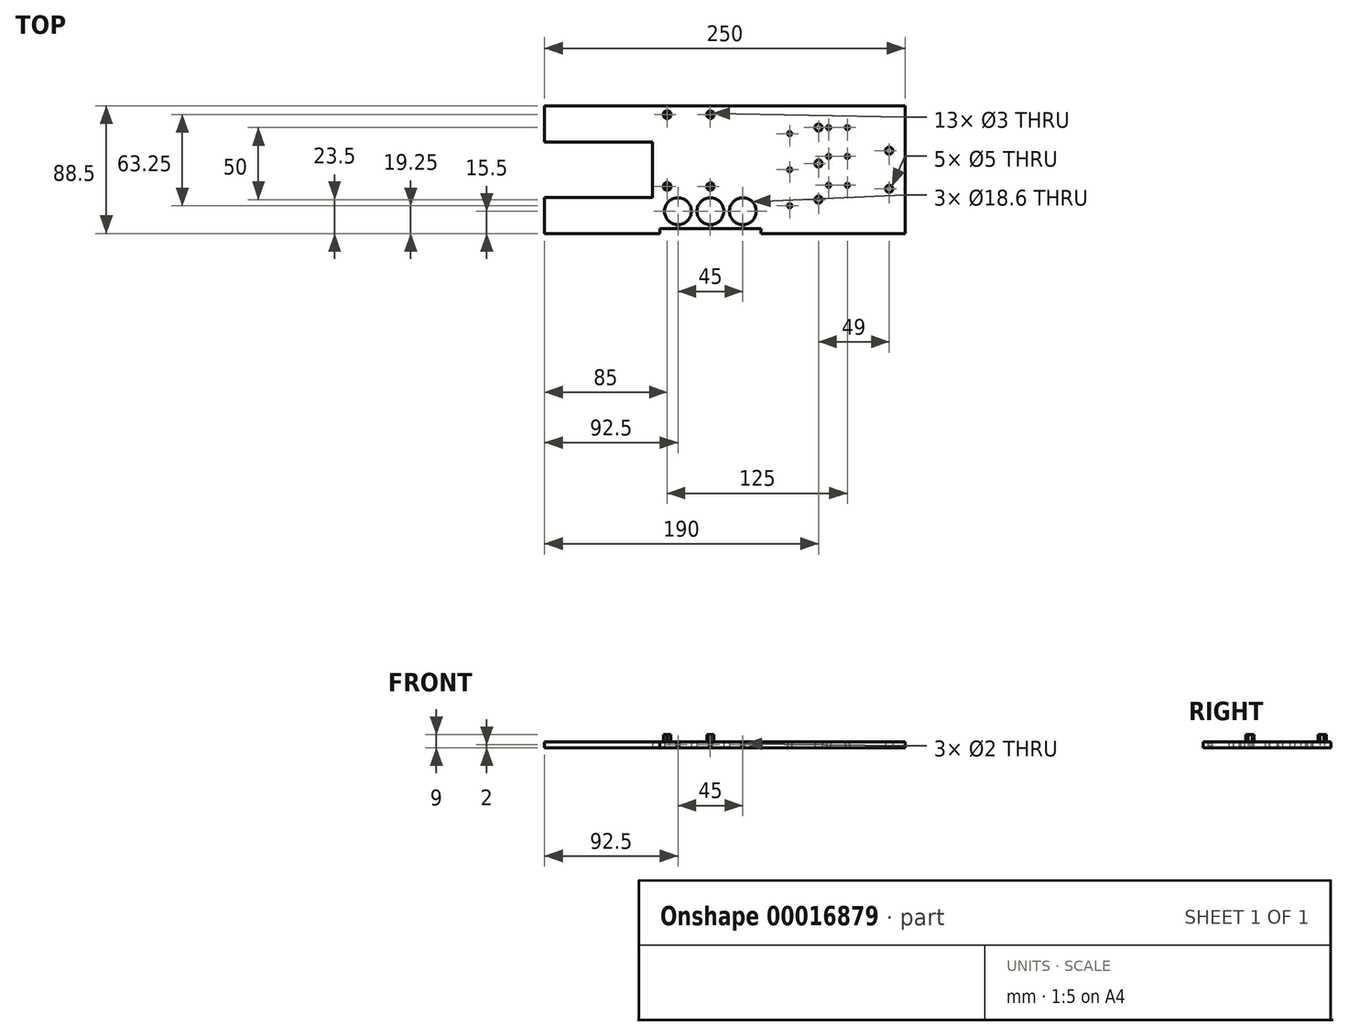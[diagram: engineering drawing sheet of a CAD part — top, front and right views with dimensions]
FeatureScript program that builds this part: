
annotation { "Feature Type Name" : "Feature", "Feature Type Description" : "" }
export const myFeature = defineFeature(function(context is Context, id is Id, definition is map)
    precondition{}
    {
        {
            var Q0;
            Q0=qCreatedBy(makeId("Top.planeOp"),FACE);
            var sketch = newSketch(context, id + "F0", { "sketchPlane" : qUnion([Q0])});
            skLineSegment(sketch, "E0", {"start": v(0, 0) * mm, "end": v(80, 0) * mm});
            skLineSegment(sketch, "E1", {"start": v(80, 0) * mm, "end": v(80, 3.5) * mm});
            skLineSegment(sketch, "E2", {"start": v(80, 3.5) * mm, "end": v(150, 3.5) * mm});
            skLineSegment(sketch, "E3", {"start": v(150, 3.5) * mm, "end": v(150, 0) * mm});
            skLineSegment(sketch, "E4", {"start": v(150, 0) * mm, "end": v(250, 0) * mm});
            skLineSegment(sketch, "E5", {"start": v(250, 0) * mm, "end": v(250, 88.5) * mm});
            skLineSegment(sketch, "E6", {"start": v(250, 88.5) * mm, "end": v(0, 88.5) * mm});
            skLineSegment(sketch, "E7", {"start": v(0, 88.5) * mm, "end": v(0, 63.5) * mm});
            skLineSegment(sketch, "E8", {"start": v(0, 63.5) * mm, "end": v(75, 63.5) * mm});
            skLineSegment(sketch, "E9", {"start": v(75, 63.5) * mm, "end": v(75, 25) * mm});
            skLineSegment(sketch, "E10", {"start": v(75, 25) * mm, "end": v(0, 25) * mm});
            skLineSegment(sketch, "E11", {"start": v(0, 25) * mm, "end": v(0, 0) * mm});
            skCircle(sketch, "E12", {"center": v(92.5, 15.5) * mm, "radius": 9.3 * mm});
            skCircle(sketch, "E13", {"center": v(115, 15.5) * mm, "radius": 9.3 * mm});
            skCircle(sketch, "E14", {"center": v(137.5, 15.5) * mm, "radius": 9.3 * mm});
            skCircle(sketch, "E15", {"center": v(239, 57.5) * mm, "radius": 2.5 * mm});
            skCircle(sketch, "E16", {"center": v(239, 31) * mm, "radius": 2.5 * mm});
            skCircle(sketch, "E17", {"center": v(197, 73.5) * mm, "radius": 1.5 * mm});
            skCircle(sketch, "E18", {"center": v(210, 73.5) * mm, "radius": 1.5 * mm});
            skLineSegment(sketch, "E19", {"start": v(250, 44.25) * mm, "end": v(-80.74, 44.25) * mm, "construction": true});
            skCircle(sketch, "E20.MirrorC", {"center": v(197, 33.5) * mm, "radius": 1.5 * mm});
            skCircle(sketch, "E21.MirrorC", {"center": v(210, 33.5) * mm, "radius": 1.5 * mm});
            skCircle(sketch, "E22", {"center": v(197, 53.5) * mm, "radius": 1.5 * mm});
            skCircle(sketch, "E23", {"center": v(210, 53.5) * mm, "radius": 1.5 * mm});
            skCircle(sketch, "E24", {"center": v(190, 73.5) * mm, "radius": 2.5 * mm});
            skCircle(sketch, "E25", {"center": v(190, 48.5) * mm, "radius": 2.5 * mm});
            skCircle(sketch, "E26", {"center": v(190, 23.5) * mm, "radius": 2.5 * mm});
            skCircle(sketch, "E27", {"center": v(170, 19.25) * mm, "radius": 1.5 * mm});
            skCircle(sketch, "E28", {"center": v(170, 44.25) * mm, "radius": 1.5 * mm});
            skCircle(sketch, "E29", {"center": v(170, 69.25) * mm, "radius": 1.5 * mm});
            skSolve(sketch);
        }
        {
            var Q0;
            Q0 = qSketchRegion(id + "F0", true);
            extrude(context, id + "F1", {"entities" : qUnion([Q0]), "depth" : 4 * mm});
        }
        {
            var Q0;
            Q0=makeQuery(id+"F1.opExtrude","SWEPT_FACE",FACE,{"disambiguationData":[OSD([sQuery(id+"F0.wireOp",EDGE,"E2")])]});
            var sketch = newSketch(context, id + "F2", { "sketchPlane" : qUnion([Q0])});
            skPoint(sketch, "E30.0", {"position": v(92.5, 0) * mm});
            skPoint(sketch, "E30.1", {"position": v(115, 0) * mm});
            skPoint(sketch, "E30.2", {"position": v(137.5, 0) * mm});
            skCircle(sketch, "E31", {"center": v(92.5, 2) * mm, "radius": 1 * mm});
            skCircle(sketch, "E32", {"center": v(115, 2) * mm, "radius": 1 * mm});
            skCircle(sketch, "E33", {"center": v(137.5, 2) * mm, "radius": 1 * mm});
            skSolve(sketch);
        }
        {
            var Q0;
            Q0 = qSketchRegion(id + "F2", true);
            extrude(context, id + "F3", {"entities" : qUnion([Q0]), "operationType" : NewBodyOperationType.REMOVE, "endBound" : BoundingType.UP_TO_NEXT, "oppositeDirection" : true, "depth" : 25 * mm});
        }
        {
            var Q0;
            Q0=makeQuery(id+"F1.opExtrude","CAP_FACE",FACE,{"disambiguationData":[OSD([sQuery(id+"F0.wireOp",EDGE,"E0"),sQuery(id+"F0.wireOp",EDGE,"E1"),sQuery(id+"F0.wireOp",EDGE,"E2"),sQuery(id+"F0.wireOp",EDGE,"E3"),sQuery(id+"F0.wireOp",EDGE,"E4"),sQuery(id+"F0.wireOp",EDGE,"E5"),sQuery(id+"F0.wireOp",EDGE,"E6"),sQuery(id+"F0.wireOp",EDGE,"E7"),sQuery(id+"F0.wireOp",EDGE,"E8"),sQuery(id+"F0.wireOp",EDGE,"E9"),sQuery(id+"F0.wireOp",EDGE,"E10"),sQuery(id+"F0.wireOp",EDGE,"E11"),sQuery(id+"F0.wireOp",EDGE,"E12"),sQuery(id+"F0.wireOp",EDGE,"E13"),sQuery(id+"F0.wireOp",EDGE,"E14"),sQuery(id+"F0.wireOp",EDGE,"E15"),sQuery(id+"F0.wireOp",EDGE,"E16"),sQuery(id+"F0.wireOp",EDGE,"4a421984-388c-4778-8cfd-64b2ba2534b6"),sQuery(id+"F0.wireOp",EDGE,"E17"),sQuery(id+"F0.wireOp",EDGE,"402fa86f-9143-4b8b-a13e-71166aee82f4"),sQuery(id+"F0.wireOp",EDGE,"E18"),sQuery(id+"F0.wireOp",EDGE,"9f3e0d40-b936-4480-b454-21914f751cbb"),sQuery(id+"F0.wireOp",EDGE,"ea4070be-86ac-4e07-94dc-6d67086c7fd0"),sQuery(id+"F0.wireOp",EDGE,"431228db-7fc8-4f03-8ea2-0f4400f562ce0.MirrorC"),sQuery(id+"F0.wireOp",EDGE,"53232193-0ba7-4fe3-a71a-7f03452151850.MirrorC"),sQuery(id+"F0.wireOp",EDGE,"E20.MirrorC"),sQuery(id+"F0.wireOp",EDGE,"E21.MirrorC"),sQuery(id+"F0.wireOp",EDGE,"28b9a74f-4e13-4495-a41d-af9b40233b3c0.MirrorC"),sQuery(id+"F0.wireOp",EDGE,"95b830d9-cd3e-44bb-837a-3bef2442fca50.MirrorC"),sQuery(id+"F0.wireOp",EDGE,"101621b3-3997-46f1-9346-ad9f52fe62e3"),sQuery(id+"F0.wireOp",EDGE,"5d99ffdf-71ce-4d62-a65a-32a693a247e0"),sQuery(id+"F0.wireOp",EDGE,"72875ce8-6458-4410-bd34-e62cef469ffd"),sQuery(id+"F0.wireOp",EDGE,"1edcefaf-f632-4f50-8d4d-05e26532ecec"),sQuery(id+"F0.wireOp",EDGE,"0031e8d8-416b-4e22-89b7-db54a3127eba0.MirrorC"),sQuery(id+"F0.wireOp",EDGE,"c55a97cf-9bee-4432-8ab8-8a13ee360a9b0.MirrorC")])],"isStart":false});
            var sketch = newSketch(context, id + "F4", { "sketchPlane" : qUnion([Q0])});
            skCircle(sketch, "E34.cCircle", {"center": v(85, 32.5) * mm, "radius": 2.5 * mm, "construction": true});
            skLineSegment(sketch, "E34.0", {"start": v(87.5, 33.94) * mm, "end": v(87.5, 31.06) * mm});
            skLineSegment(sketch, "E34.1", {"start": v(87.5, 31.06) * mm, "end": v(85, 29.61) * mm});
            skLineSegment(sketch, "E34.2", {"start": v(85, 29.61) * mm, "end": v(82.5, 31.06) * mm});
            skLineSegment(sketch, "E34.3", {"start": v(82.5, 31.06) * mm, "end": v(82.5, 33.94) * mm});
            skLineSegment(sketch, "E34.4", {"start": v(82.5, 33.94) * mm, "end": v(85, 35.39) * mm});
            skLineSegment(sketch, "E34.5", {"start": v(85, 35.39) * mm, "end": v(87.5, 33.94) * mm});
            skPoint(sketch, "E34.0.midPoint", {"position": v(87.5, 32.5) * mm});
            skLineSegment(sketch, "E35.0", {"start": v(87.5, 83.94) * mm, "end": v(87.5, 81.06) * mm});
            skLineSegment(sketch, "E35.3", {"start": v(82.5, 81.06) * mm, "end": v(82.5, 83.94) * mm});
            skLineSegment(sketch, "E35.4", {"start": v(82.5, 83.94) * mm, "end": v(85, 85.39) * mm});
            skLineSegment(sketch, "E35.2", {"start": v(85, 79.61) * mm, "end": v(82.5, 81.06) * mm});
            skLineSegment(sketch, "E35.5", {"start": v(85, 85.39) * mm, "end": v(87.5, 83.94) * mm});
            skLineSegment(sketch, "E35.1", {"start": v(87.5, 81.06) * mm, "end": v(85, 79.61) * mm});
            skCircle(sketch, "E35.cCircle", {"center": v(85, 82.5) * mm, "radius": 2.5 * mm, "construction": true});
            skPoint(sketch, "E35.0.midPoint", {"position": v(87.5, 82.5) * mm});
            skLineSegment(sketch, "E36", {"start": v(100, 108.07) * mm, "end": v(100, -15.28) * mm, "construction": true});
            skLineSegment(sketch, "E37.MirrorCS", {"start": v(112.5, 83.94) * mm, "end": v(112.5, 81.06) * mm});
            skLineSegment(sketch, "E38.MirrorCS", {"start": v(115, 79.61) * mm, "end": v(117.5, 81.06) * mm});
            skLineSegment(sketch, "E39.MirrorCS", {"start": v(117.5, 81.06) * mm, "end": v(117.5, 83.94) * mm});
            skPoint(sketch, "E40.MirrorP", {"position": v(112.5, 82.5) * mm});
            skLineSegment(sketch, "E41.MirrorCS", {"start": v(112.5, 81.06) * mm, "end": v(115, 79.61) * mm});
            skLineSegment(sketch, "E42.MirrorCS", {"start": v(115, 85.39) * mm, "end": v(112.5, 83.94) * mm});
            skCircle(sketch, "E43.MirrorC", {"center": v(115, 82.5) * mm, "radius": 2.5 * mm});
            skLineSegment(sketch, "E44.MirrorCS", {"start": v(117.5, 83.94) * mm, "end": v(115, 85.39) * mm});
            skCircle(sketch, "E45.MirrorC", {"center": v(115, 32.5) * mm, "radius": 2.5 * mm});
            skLineSegment(sketch, "E46.MirrorCS", {"start": v(112.5, 33.94) * mm, "end": v(112.5, 31.06) * mm});
            skLineSegment(sketch, "E47.MirrorCS", {"start": v(112.5, 31.06) * mm, "end": v(115, 29.61) * mm});
            skLineSegment(sketch, "E48.MirrorCS", {"start": v(115, 29.61) * mm, "end": v(117.5, 31.06) * mm});
            skLineSegment(sketch, "E49.MirrorCS", {"start": v(117.5, 31.06) * mm, "end": v(117.5, 33.94) * mm});
            skLineSegment(sketch, "E50.MirrorCS", {"start": v(115, 35.39) * mm, "end": v(112.5, 33.94) * mm});
            skPoint(sketch, "E51.MirrorP", {"position": v(112.5, 32.5) * mm});
            skLineSegment(sketch, "E52.MirrorCS", {"start": v(117.5, 33.94) * mm, "end": v(115, 35.39) * mm});
            skCircle(sketch, "E53", {"center": v(85, 32.5) * mm, "radius": 1.5 * mm});
            skCircle(sketch, "E54", {"center": v(115, 32.5) * mm, "radius": 1.5 * mm});
            skCircle(sketch, "E55", {"center": v(85, 82.5) * mm, "radius": 1.5 * mm});
            skCircle(sketch, "E56", {"center": v(115, 82.5) * mm, "radius": 1.5 * mm});
            skSolve(sketch);
        }
        {
            var Q0;
            Q0 = qSketchRegion(id + "F4", true);
            extrude(context, id + "F5", {"entities" : qUnion([Q0]), "depth" : 5 * mm});
        }
        {
            var Q0;
            Q0=makeQuery(id+"F1.opExtrude","SWEPT_BODY",BODY,{"disambiguationData":[OSD([sQuery(id+"F0.wireOp",EDGE,"E0"),sQuery(id+"F0.wireOp",EDGE,"E1"),sQuery(id+"F0.wireOp",EDGE,"E2"),sQuery(id+"F0.wireOp",EDGE,"E3"),sQuery(id+"F0.wireOp",EDGE,"E4"),sQuery(id+"F0.wireOp",EDGE,"E5"),sQuery(id+"F0.wireOp",EDGE,"E6"),sQuery(id+"F0.wireOp",EDGE,"E7"),sQuery(id+"F0.wireOp",EDGE,"E8"),sQuery(id+"F0.wireOp",EDGE,"E9"),sQuery(id+"F0.wireOp",EDGE,"E10"),sQuery(id+"F0.wireOp",EDGE,"E11"),sQuery(id+"F0.wireOp",EDGE,"E12"),sQuery(id+"F0.wireOp",EDGE,"E13"),sQuery(id+"F0.wireOp",EDGE,"E14"),sQuery(id+"F0.wireOp",EDGE,"E15"),sQuery(id+"F0.wireOp",EDGE,"E16"),sQuery(id+"F0.wireOp",EDGE,"4a421984-388c-4778-8cfd-64b2ba2534b6"),sQuery(id+"F0.wireOp",EDGE,"E17"),sQuery(id+"F0.wireOp",EDGE,"402fa86f-9143-4b8b-a13e-71166aee82f4"),sQuery(id+"F0.wireOp",EDGE,"E18"),sQuery(id+"F0.wireOp",EDGE,"9f3e0d40-b936-4480-b454-21914f751cbb"),sQuery(id+"F0.wireOp",EDGE,"ea4070be-86ac-4e07-94dc-6d67086c7fd0"),sQuery(id+"F0.wireOp",EDGE,"431228db-7fc8-4f03-8ea2-0f4400f562ce0.MirrorC"),sQuery(id+"F0.wireOp",EDGE,"53232193-0ba7-4fe3-a71a-7f03452151850.MirrorC"),sQuery(id+"F0.wireOp",EDGE,"E20.MirrorC"),sQuery(id+"F0.wireOp",EDGE,"E21.MirrorC"),sQuery(id+"F0.wireOp",EDGE,"28b9a74f-4e13-4495-a41d-af9b40233b3c0.MirrorC"),sQuery(id+"F0.wireOp",EDGE,"95b830d9-cd3e-44bb-837a-3bef2442fca50.MirrorC"),sQuery(id+"F0.wireOp",EDGE,"101621b3-3997-46f1-9346-ad9f52fe62e3"),sQuery(id+"F0.wireOp",EDGE,"5d99ffdf-71ce-4d62-a65a-32a693a247e0"),sQuery(id+"F0.wireOp",EDGE,"72875ce8-6458-4410-bd34-e62cef469ffd"),sQuery(id+"F0.wireOp",EDGE,"1edcefaf-f632-4f50-8d4d-05e26532ecec"),sQuery(id+"F0.wireOp",EDGE,"0031e8d8-416b-4e22-89b7-db54a3127eba0.MirrorC"),sQuery(id+"F0.wireOp",EDGE,"c55a97cf-9bee-4432-8ab8-8a13ee360a9b0.MirrorC")])]});
            var Q1;
            Q1=makeQuery(id+"F5.opExtrude","SWEPT_BODY",BODY,{"disambiguationData":[OSD([sQuery(id+"F4.wireOp",EDGE,"E34.0"),sQuery(id+"F4.wireOp",EDGE,"E34.1"),sQuery(id+"F4.wireOp",EDGE,"E34.2"),sQuery(id+"F4.wireOp",EDGE,"E34.3"),sQuery(id+"F4.wireOp",EDGE,"E34.4"),sQuery(id+"F4.wireOp",EDGE,"E34.5")])]});
            var Q2;
            Q2=makeQuery(id+"F5.opExtrude","SWEPT_BODY",BODY,{"disambiguationData":[OSD([sQuery(id+"F4.wireOp",EDGE,"33c3f6af-82dd-4364-b386-9f01c39b1b5f0.MirrorCS"),sQuery(id+"F4.wireOp",EDGE,"33c3f6af-82dd-4364-b386-9f01c39b1b5f3.MirrorCS"),sQuery(id+"F4.wireOp",EDGE,"33c3f6af-82dd-4364-b386-9f01c39b1b5f4.MirrorCS"),sQuery(id+"F4.wireOp",EDGE,"33c3f6af-82dd-4364-b386-9f01c39b1b5f5.MirrorCS"),sQuery(id+"F4.wireOp",EDGE,"33c3f6af-82dd-4364-b386-9f01c39b1b5f6.MirrorCS"),sQuery(id+"F4.wireOp",EDGE,"33c3f6af-82dd-4364-b386-9f01c39b1b5f7.MirrorCS")])]});
            var Q3;
            Q3=makeQuery(id+"F5.opExtrude","SWEPT_BODY",BODY,{"disambiguationData":[OSD([sQuery(id+"F4.wireOp",EDGE,"E37.MirrorCS"),sQuery(id+"F4.wireOp",EDGE,"E38.MirrorCS"),sQuery(id+"F4.wireOp",EDGE,"E39.MirrorCS"),sQuery(id+"F4.wireOp",EDGE,"E41.MirrorCS"),sQuery(id+"F4.wireOp",EDGE,"E42.MirrorCS"),sQuery(id+"F4.wireOp",EDGE,"E44.MirrorCS")])]});
            var Q4;
            Q4=makeQuery(id+"F5.opExtrude","SWEPT_BODY",BODY,{"disambiguationData":[OSD([sQuery(id+"F4.wireOp",EDGE,"E46.MirrorCS"),sQuery(id+"F4.wireOp",EDGE,"E47.MirrorCS"),sQuery(id+"F4.wireOp",EDGE,"E48.MirrorCS"),sQuery(id+"F4.wireOp",EDGE,"E49.MirrorCS"),sQuery(id+"F4.wireOp",EDGE,"E50.MirrorCS"),sQuery(id+"F4.wireOp",EDGE,"E52.MirrorCS")])]});
            var Q5;
            Q5=makeQuery(id+"F5.opExtrude","SWEPT_BODY",BODY,{"disambiguationData":[OSD([sQuery(id+"F4.wireOp",EDGE,"E35.0"),sQuery(id+"F4.wireOp",EDGE,"E35.3"),sQuery(id+"F4.wireOp",EDGE,"E35.4"),sQuery(id+"F4.wireOp",EDGE,"E35.2"),sQuery(id+"F4.wireOp",EDGE,"E35.5"),sQuery(id+"F4.wireOp",EDGE,"E35.1")])]});
            booleanBodies(context, id + "F6", {"operationType" : BooleanOperationType.UNION, "tools" : qUnion([Q0, Q1, Q2, Q3, Q4, Q5])});
        }
        {
            var Q0;
            Q0=makeQuery(id+"F6.opBoolean","SPLIT",FACE,{"disambiguationData":[TD([makeQuery(id+"F5.opExtrude","SWEPT_FACE",FACE,{"disambiguationData":[OSD([sQuery(id+"F4.wireOp",EDGE,"E56")])]})])],"derivedFrom":makeQuery(id+"F1.opExtrude","CAP_FACE",FACE,{"disambiguationData":[OSD([sQuery(id+"F0.wireOp",EDGE,"E0"),sQuery(id+"F0.wireOp",EDGE,"E1"),sQuery(id+"F0.wireOp",EDGE,"E2"),sQuery(id+"F0.wireOp",EDGE,"E3"),sQuery(id+"F0.wireOp",EDGE,"E4"),sQuery(id+"F0.wireOp",EDGE,"E5"),sQuery(id+"F0.wireOp",EDGE,"E6"),sQuery(id+"F0.wireOp",EDGE,"E7"),sQuery(id+"F0.wireOp",EDGE,"E8"),sQuery(id+"F0.wireOp",EDGE,"E9"),sQuery(id+"F0.wireOp",EDGE,"E10"),sQuery(id+"F0.wireOp",EDGE,"E11"),sQuery(id+"F0.wireOp",EDGE,"E12"),sQuery(id+"F0.wireOp",EDGE,"E13"),sQuery(id+"F0.wireOp",EDGE,"E14"),sQuery(id+"F0.wireOp",EDGE,"E15"),sQuery(id+"F0.wireOp",EDGE,"E16"),sQuery(id+"F0.wireOp",EDGE,"E17"),sQuery(id+"F0.wireOp",EDGE,"E18"),sQuery(id+"F0.wireOp",EDGE,"E20.MirrorC"),sQuery(id+"F0.wireOp",EDGE,"E21.MirrorC"),sQuery(id+"F0.wireOp",EDGE,"E22"),sQuery(id+"F0.wireOp",EDGE,"E23"),sQuery(id+"F0.wireOp",EDGE,"E24"),sQuery(id+"F0.wireOp",EDGE,"E25"),sQuery(id+"F0.wireOp",EDGE,"E26"),sQuery(id+"F0.wireOp",EDGE,"E27"),sQuery(id+"F0.wireOp",EDGE,"E28"),sQuery(id+"F0.wireOp",EDGE,"E29")])],"isStart":false})});
            var Q1;
            Q1=makeQuery(id+"F6.opBoolean","SPLIT",FACE,{"disambiguationData":[TD([makeQuery(id+"F5.opExtrude","SWEPT_FACE",FACE,{"disambiguationData":[OSD([sQuery(id+"F4.wireOp",EDGE,"E55")])]})])],"derivedFrom":makeQuery(id+"F1.opExtrude","CAP_FACE",FACE,{"disambiguationData":[OSD([sQuery(id+"F0.wireOp",EDGE,"E0"),sQuery(id+"F0.wireOp",EDGE,"E1"),sQuery(id+"F0.wireOp",EDGE,"E2"),sQuery(id+"F0.wireOp",EDGE,"E3"),sQuery(id+"F0.wireOp",EDGE,"E4"),sQuery(id+"F0.wireOp",EDGE,"E5"),sQuery(id+"F0.wireOp",EDGE,"E6"),sQuery(id+"F0.wireOp",EDGE,"E7"),sQuery(id+"F0.wireOp",EDGE,"E8"),sQuery(id+"F0.wireOp",EDGE,"E9"),sQuery(id+"F0.wireOp",EDGE,"E10"),sQuery(id+"F0.wireOp",EDGE,"E11"),sQuery(id+"F0.wireOp",EDGE,"E12"),sQuery(id+"F0.wireOp",EDGE,"E13"),sQuery(id+"F0.wireOp",EDGE,"E14"),sQuery(id+"F0.wireOp",EDGE,"E15"),sQuery(id+"F0.wireOp",EDGE,"E16"),sQuery(id+"F0.wireOp",EDGE,"E17"),sQuery(id+"F0.wireOp",EDGE,"E18"),sQuery(id+"F0.wireOp",EDGE,"E20.MirrorC"),sQuery(id+"F0.wireOp",EDGE,"E21.MirrorC"),sQuery(id+"F0.wireOp",EDGE,"E22"),sQuery(id+"F0.wireOp",EDGE,"E23"),sQuery(id+"F0.wireOp",EDGE,"E24"),sQuery(id+"F0.wireOp",EDGE,"E25"),sQuery(id+"F0.wireOp",EDGE,"E26"),sQuery(id+"F0.wireOp",EDGE,"E27"),sQuery(id+"F0.wireOp",EDGE,"E28"),sQuery(id+"F0.wireOp",EDGE,"E29")])],"isStart":false})});
            var Q2;
            Q2=makeQuery(id+"F6.opBoolean","SPLIT",FACE,{"disambiguationData":[TD([makeQuery(id+"F5.opExtrude","SWEPT_FACE",FACE,{"disambiguationData":[OSD([sQuery(id+"F4.wireOp",EDGE,"E53")])]})])],"derivedFrom":makeQuery(id+"F1.opExtrude","CAP_FACE",FACE,{"disambiguationData":[OSD([sQuery(id+"F0.wireOp",EDGE,"E0"),sQuery(id+"F0.wireOp",EDGE,"E1"),sQuery(id+"F0.wireOp",EDGE,"E2"),sQuery(id+"F0.wireOp",EDGE,"E3"),sQuery(id+"F0.wireOp",EDGE,"E4"),sQuery(id+"F0.wireOp",EDGE,"E5"),sQuery(id+"F0.wireOp",EDGE,"E6"),sQuery(id+"F0.wireOp",EDGE,"E7"),sQuery(id+"F0.wireOp",EDGE,"E8"),sQuery(id+"F0.wireOp",EDGE,"E9"),sQuery(id+"F0.wireOp",EDGE,"E10"),sQuery(id+"F0.wireOp",EDGE,"E11"),sQuery(id+"F0.wireOp",EDGE,"E12"),sQuery(id+"F0.wireOp",EDGE,"E13"),sQuery(id+"F0.wireOp",EDGE,"E14"),sQuery(id+"F0.wireOp",EDGE,"E15"),sQuery(id+"F0.wireOp",EDGE,"E16"),sQuery(id+"F0.wireOp",EDGE,"E17"),sQuery(id+"F0.wireOp",EDGE,"E18"),sQuery(id+"F0.wireOp",EDGE,"E20.MirrorC"),sQuery(id+"F0.wireOp",EDGE,"E21.MirrorC"),sQuery(id+"F0.wireOp",EDGE,"E22"),sQuery(id+"F0.wireOp",EDGE,"E23"),sQuery(id+"F0.wireOp",EDGE,"E24"),sQuery(id+"F0.wireOp",EDGE,"E25"),sQuery(id+"F0.wireOp",EDGE,"E26"),sQuery(id+"F0.wireOp",EDGE,"E27"),sQuery(id+"F0.wireOp",EDGE,"E28"),sQuery(id+"F0.wireOp",EDGE,"E29")])],"isStart":false})});
            var Q3;
            Q3=makeQuery(id+"F6.opBoolean","SPLIT",FACE,{"disambiguationData":[TD([makeQuery(id+"F5.opExtrude","SWEPT_FACE",FACE,{"disambiguationData":[OSD([sQuery(id+"F4.wireOp",EDGE,"E54")])]})])],"derivedFrom":makeQuery(id+"F1.opExtrude","CAP_FACE",FACE,{"disambiguationData":[OSD([sQuery(id+"F0.wireOp",EDGE,"E0"),sQuery(id+"F0.wireOp",EDGE,"E1"),sQuery(id+"F0.wireOp",EDGE,"E2"),sQuery(id+"F0.wireOp",EDGE,"E3"),sQuery(id+"F0.wireOp",EDGE,"E4"),sQuery(id+"F0.wireOp",EDGE,"E5"),sQuery(id+"F0.wireOp",EDGE,"E6"),sQuery(id+"F0.wireOp",EDGE,"E7"),sQuery(id+"F0.wireOp",EDGE,"E8"),sQuery(id+"F0.wireOp",EDGE,"E9"),sQuery(id+"F0.wireOp",EDGE,"E10"),sQuery(id+"F0.wireOp",EDGE,"E11"),sQuery(id+"F0.wireOp",EDGE,"E12"),sQuery(id+"F0.wireOp",EDGE,"E13"),sQuery(id+"F0.wireOp",EDGE,"E14"),sQuery(id+"F0.wireOp",EDGE,"E15"),sQuery(id+"F0.wireOp",EDGE,"E16"),sQuery(id+"F0.wireOp",EDGE,"E17"),sQuery(id+"F0.wireOp",EDGE,"E18"),sQuery(id+"F0.wireOp",EDGE,"E20.MirrorC"),sQuery(id+"F0.wireOp",EDGE,"E21.MirrorC"),sQuery(id+"F0.wireOp",EDGE,"E22"),sQuery(id+"F0.wireOp",EDGE,"E23"),sQuery(id+"F0.wireOp",EDGE,"E24"),sQuery(id+"F0.wireOp",EDGE,"E25"),sQuery(id+"F0.wireOp",EDGE,"E26"),sQuery(id+"F0.wireOp",EDGE,"E27"),sQuery(id+"F0.wireOp",EDGE,"E28"),sQuery(id+"F0.wireOp",EDGE,"E29")])],"isStart":false})});
            extrude(context, id + "F7", {"entities" : qUnion([Q0, Q1, Q2, Q3]), "operationType" : NewBodyOperationType.REMOVE, "oppositeDirection" : true, "depth" : 25 * mm});
        }
    });
